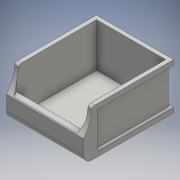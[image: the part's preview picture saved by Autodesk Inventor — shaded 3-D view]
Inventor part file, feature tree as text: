
AUTODESK INVENTOR PART (.ipt)
format: ipt  version: 2016 (Build 200138000, 138)  size: 173,568 bytes
history: native  units: mm
features: extrude x6, sketch x6, fillet x3, plane x1, mirror x1
ambient origin geometry x8: Origin, YZ Plane, XZ Plane, XY Plane, X Axis, Y Axis, Z Axis, Center Point
bodies: Solid1 (feature_tree)
feature tree (17):
  extrude  "Extrusion1"  Depth=160.0mm
  extrude  "Extrusion2"  Depth=7.0mm
  extrude  "Extrusion3"  Depth=7.0mm
  extrude  "Extrusion4"  Depth=78.0mm TaperAngle=0.0deg
  plane  "Work Plane1"
  mirror  "Mirror1"
  extrude  "Extrusion5"  TaperAngle=120.0deg  [1 undecoded]
  fillet  "Fillet1"  Radius=40.0mm
  fillet  "Fillet2"  Radius=9.0mm
  extrude  "Extrusion6"  TaperAngle=0.0deg  [1 undecoded]
  fillet  "Fillet3"  Radius=25.0mm
  sketch  "Sketch1"  dims[d0=137.0mm d1=160.0mm]
  sketch  "Sketch2"  dims[d2=82.0mm d3=0.0mm d4=7.0mm]
  sketch  "Sketch3"  dims[d5=7.0mm d6=7.0mm]
  sketch  "Sketch4"  dims[d7=11.0mm d8=78.0mm d9=0.0mm]
  sketch  "Sketch5"  dims[d10=60.0deg d11=120.0deg d12=40.0mm d13=0.0mm d14=9.0mm]
  sketch  "Sketch6"  dims[d15=9.0mm d16=0.0mm d17=25.0mm d18=5.0mm d19=0.0mm d20=5.0mm d21=0.0mm d22=15.0mm d23=15.0mm d24=130.0mm d25=50.0mm d26=0.0mm d27=0.0mm d28=0.0mm d29=5.0mm]
note: 2 required parameter values undecoded (feature->parameter linkage not recoverable at this tier; creation-order binding heuristic only, values carry confidence <= 0.55)
